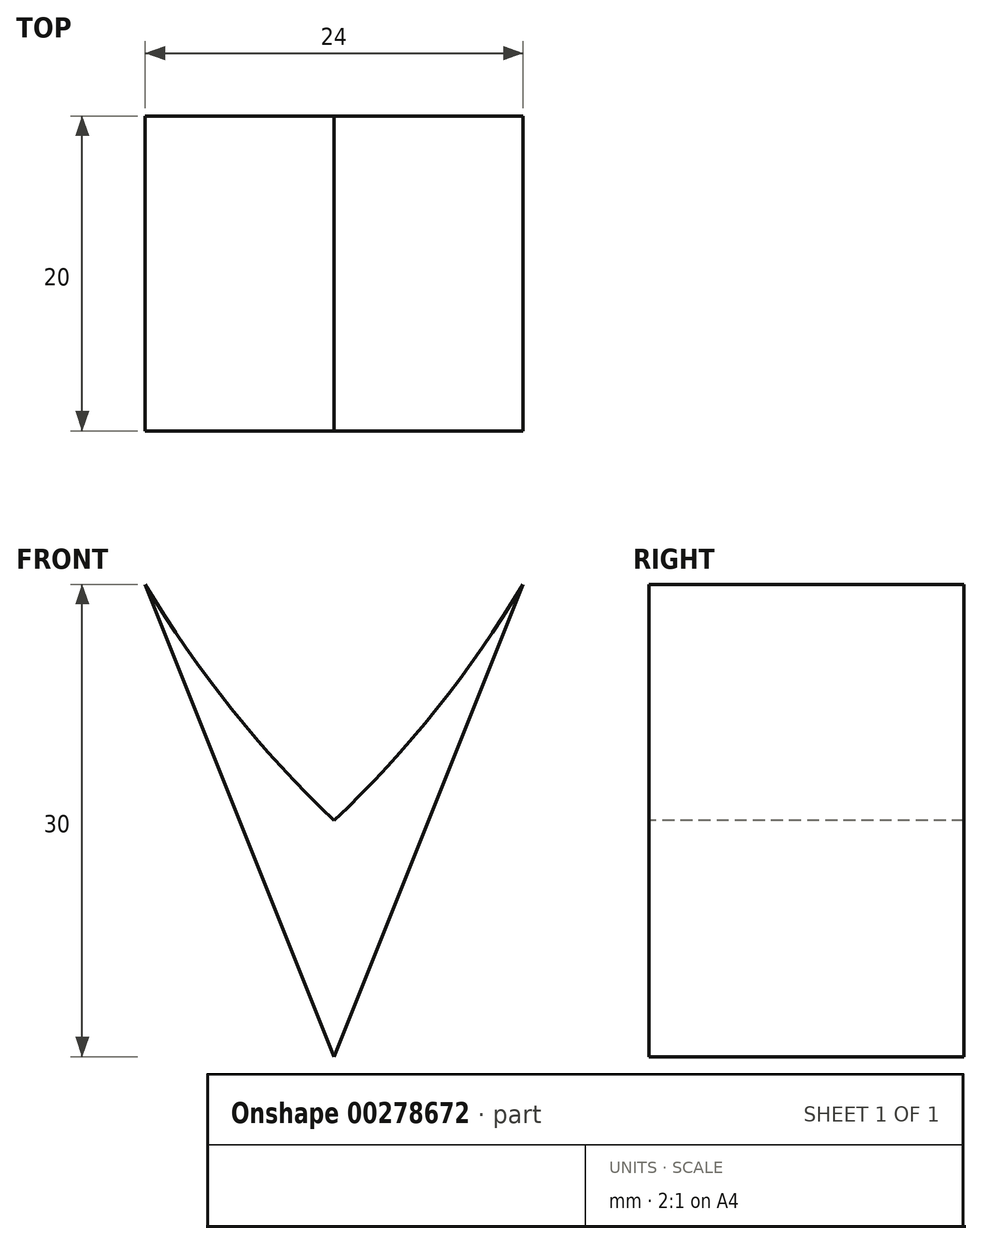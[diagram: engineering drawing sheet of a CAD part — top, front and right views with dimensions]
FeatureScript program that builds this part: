
annotation { "Feature Type Name" : "Feature", "Feature Type Description" : "" }
export const myFeature = defineFeature(function(context is Context, id is Id, definition is map)
    precondition{}
    {
        {
            var Q0;
            Q0=qCreatedBy(makeId("Front.planeOp"),FACE);
            var sketch = newSketch(context, id + "F0", { "sketchPlane" : qUnion([Q0])});
            skLineSegment(sketch, "E0.bottom", {"start": v(-12, 15) * mm, "end": v(12, 15) * mm});
            skLineSegment(sketch, "E0.top", {"start": v(-12, -15) * mm, "end": v(12, -15) * mm});
            skLineSegment(sketch, "E0.left", {"start": v(-12, 15) * mm, "end": v(-12, -15) * mm});
            skLineSegment(sketch, "E0.right", {"start": v(12, 15) * mm, "end": v(12, -15) * mm});
            skSolve(sketch);
        }
        {
            var Q0;
            Q0 = qSketchRegion(id + "F0", true);
            extrude(context, id + "F1", {"entities" : qUnion([Q0]), "depth" : 20 * mm});
        }
        {
            var Q0;
            Q0=makeQuery(id+"F1.opExtrude","CAP_FACE",FACE,{"disambiguationData":[OSD([sQuery(id+"F0.wireOp",EDGE,"E0.bottom"),sQuery(id+"F0.wireOp",EDGE,"E0.top"),sQuery(id+"F0.wireOp",EDGE,"E0.left"),sQuery(id+"F0.wireOp",EDGE,"E0.right")])],"isStart":false});
            var sketch = newSketch(context, id + "F2", { "sketchPlane" : qUnion([Q0])});
            skArc(sketch, "E1", {"start": v(0, 0) * mm, "mid": v(6.52, 7.09) * mm, "end": v(12, 15) * mm});
            skArc(sketch, "E2", {"start": v(-12, 15) * mm, "mid": v(-6.52, 7.09) * mm, "end": v(0, 0) * mm});
            skLineSegment(sketch, "E3", {"start": v(-12, 15) * mm, "end": v(12, 15) * mm});
            skSolve(sketch);
        }
        {
            var Q0;
            Q0 = qSketchRegion(id + "F2", true);
            extrude(context, id + "F3", {"entities" : qUnion([Q0]), "operationType" : NewBodyOperationType.REMOVE, "oppositeDirection" : true, "depth" : 25 * mm});
        }
        {
            var Q0;
            Q0=makeQuery(id+"F1.opExtrude","CAP_FACE",FACE,{"disambiguationData":[OSD([sQuery(id+"F0.wireOp",EDGE,"E0.bottom"),sQuery(id+"F0.wireOp",EDGE,"E0.top"),sQuery(id+"F0.wireOp",EDGE,"E0.left"),sQuery(id+"F0.wireOp",EDGE,"E0.right")])],"isStart":false});
            var sketch = newSketch(context, id + "F4", { "sketchPlane" : qUnion([Q0])});
            skLineSegment(sketch, "E4", {"start": v(-12, 15) * mm, "end": v(0, -15) * mm});
            skLineSegment(sketch, "E5", {"start": v(0, -15) * mm, "end": v(12, 15) * mm});
            skLineSegment(sketch, "E6", {"start": v(12, 15) * mm, "end": v(12, -15) * mm});
            skLineSegment(sketch, "E7", {"start": v(12, -15) * mm, "end": v(-12, -15) * mm});
            skLineSegment(sketch, "E8", {"start": v(-12, -15) * mm, "end": v(-12, 15) * mm});
            skSolve(sketch);
        }
        {
            var Q0;
            Q0 = qSketchRegion(id + "F4", true);
            extrude(context, id + "F5", {"entities" : qUnion([Q0]), "operationType" : NewBodyOperationType.REMOVE, "oppositeDirection" : true, "depth" : 25 * mm});
        }
    });
